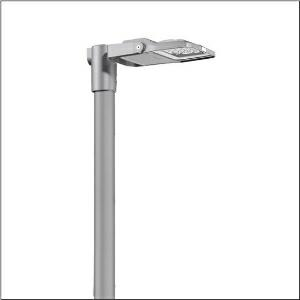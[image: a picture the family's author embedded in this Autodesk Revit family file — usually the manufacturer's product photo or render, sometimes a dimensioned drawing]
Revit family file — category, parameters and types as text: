
# Revit family: floodlight_fl_21_iq_micro___pl43_5xa7761a2a3a_2bb2
name_source: partatom
category: Lighting Fixtures
units: mm (PartAtom-declared; Revit-internal decimal feet)

## family parameters
Cut with Voids When Loaded = No
Host = Face
Light Source = No
Part Type = Normal
Room Calculation Point = No
Round Connector Dimension = Use Diameter
Shared = No

## types (1)
- --- (1 x LED, 3040 lm, 23.1 W, 3000K)
    Apparent Load = 23 VA
    CIE Flux Codes = 29 80 99 100 100
    Color Rendering = 70
    Color Temperature = 3000K
    Default Elevation = 1800 mm
    Description = Floodlight FL 21 iQ micro, floodlight, primary light control with lens, of PMMA, primary optical cover: protective disc, of toughened safety glass, transparent, light distribution: PL43, light emission: direct distribution, installation type: surface-mounted, LED, High Power LED, rated luminous flux: 3.040lm, luminous efficacy: 132lm/W, light colour: 730, colour temperature: 3000K, control gear: iQ Comfort/DALI, control: optimised constant luminous flux control (CLO 2.0), Desk-Remote (wireless, voltage-free reading and setting of iQ features in the workshop via application-optimized NFC function/RFID function), Light-Fading, Smart-Wire, Night-Set, Lumen-Switch, Temp-Guard, Auto-Match, with terminal, 6-pole, mains connection: 220..240V, AC, 50/60Hz, start of lifetime: 23W, end of service life: 24W, reduction: 11W, luminaire housing, of diecast aluminium, powder-coated, Siteco® metallic grey (DB 702S), corrosivity category C5 mid according to DIN EN ISO 12944, suitable for swimming pools, chlorine-resistant, sealing non-destructively replaceable, please order mast flange separately, mast bracket, of steel, galvanised, powder-coated, Siteco® metallic grey (DB 702S), protection rating (complete): IP66, insulation class (complete): insulation class II (safety insulation), certification: CE, ENEC, VDE, protection symbol: D, impact resistance: IK07, permissible operating ambient temperature: -40..+40°C, permissible operating ambient temperature for outdoor applications: -40..+50°C, standard: DIN EN 12944, LABS conformity tested according to VDMA 24364:2018-05, packaging unit: 1 piece

Light Distribution: PL43
    Height = 65 mm
    Lamp = 1 x LED
    Lamp Light Flux = 3040 lm
    Lamp Power = 23.1 W
    Lamp count = 1
    Length = 312 mm
    Luminous efficacy = 132 lm/W
    Manufacturer = Siteco
    ModVariant = No
    Model = 5XA7761A2A3A
    Number of Poles = 1
    OnlyDefault = Yes
    Power Factor = 1
    Product Name = Floodlight FL 21 iQ micro | PL43
    Product group = floodlight | pylon top
    ProductGroupID = 6101
    Protection Class = Protection class II
    Protection Degree = IP 66
    RLX_Detail_Level = 1
    RLX_Emergency_Light_Flux = 0 lm
    RLX_Emergency_Type = 0
    RLX_Emergency_Type_DB = No
    RlxData = <blob elided: 101813 chars, md5=31ca4085>
    Socket = socket
    Standby Power = 0 W
    System Light Flux = 3040 lm
    System Power = 23 W
    Type Comments = factory setting: luminous flux: 100 % | dim-lin: 254 | 455 mA
    Type Image = l_1007121.jpg
    URL = http://relux.com
    VarID = @adj_176828
    Voltage = 0 V
    Weight = 0.00 kg
    Width = 230 mm

## geometry (parser evidence)
native form markers: Blend x4, Sweep x12
no freeform markers — native parametric forms only
